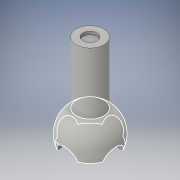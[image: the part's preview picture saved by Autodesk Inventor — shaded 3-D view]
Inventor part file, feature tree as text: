
AUTODESK INVENTOR PART (.ipt)
format: ipt  version: 2016 (Build 200138000, 138)  size: 165,376 bytes
history: native  units: in
note: dims shown in document units (in); Inventor stores cm internally (conversion verified against a paired STEP export)
features: sketch x4, extrude x3, revolve x1
ambient origin geometry x8: Origin, YZ Plane, XZ Plane, XY Plane, X Axis, Y Axis, Z Axis, Center Point
bodies: Solid1 (feature_tree)
feature tree (8):
  revolve  "Revolution1"  [1 undecoded]
  extrude  "Extrusion1"  Depth=0.225in
  extrude  "Extrusion2"  Depth=0.32in
  extrude  "Extrusion3"  Depth=100.0in TaperAngle=0.0deg
  sketch  "Sketch1"  dims[d1=0.83in d2=0.06in]
  sketch  "Sketch4"  dims[d3=90.0deg d4=0.225in]
  sketch  "Sketch5"  dims[d5=0.05in d6=0.0in d7=0.32in]
  sketch  "Sketch7"  dims[d8=100.0in d9=0.0in d10=100.0in d11=0.0in d12=1.33in]
note: 1 required parameter value undecoded (feature->parameter linkage not recoverable at this tier; creation-order binding heuristic only, values carry confidence <= 0.55)
